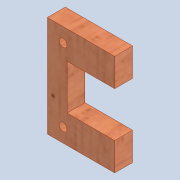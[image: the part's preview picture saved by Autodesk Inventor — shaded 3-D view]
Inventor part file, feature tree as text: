
AUTODESK INVENTOR PART (.ipt)
format: ipt  version: 2020 (Build 240168000, 168)  size: 214,528 bytes
history: native  units: mm
features: other x4, extrude x3, sketch x3, reference x1
ambient origin geometry x8: Origin, YZ Plane, XZ Plane, XY Plane, X Axis, Y Axis, Z Axis, Center Point
bodies: Solid1 (feature_tree)
feature tree (11):
  extrude  "Extrusion1"  Depth=45.0mm
  extrude  "Extrusion3"  TaperAngle=0.0deg  [1 undecoded]
  extrude  "Extrusion4"  Depth=10.0mm TaperAngle=0.0deg
  sketch  "Sketch1"  dims[d0=30.0mm d1=45.0mm]
  sketch  "Sketch3"  dims[d2=8.0mm d3=0.0mm d8=0.0mm]
  reference  "Reference1"
  sketch  "Sketch4"  dims[d9=20.0mm d10=10.0mm d11=0.0mm d15=0.0mm d16=0.0mm d17=3.5mm d18=3.5mm d19=5.0mm d20=7.0mm d21=5.0mm d22=35.0mm]
  parser-record x1  (decoder bookkeeping rows leaked as tree rows — omitted from the tree; the rows remain in map.json)
  other  "0005-00-00 Ansamblu_General.iam"
  other  "Plunger Assembly_Défaut:1"
  other  "plunger_Défaut_4"
note: 1 required parameter value undecoded (feature->parameter linkage not recoverable at this tier; creation-order binding heuristic only, values carry confidence <= 0.55)
note: 1 file-system path scrubbed to <path> (originals preserved in map.json)
